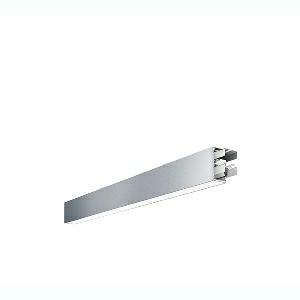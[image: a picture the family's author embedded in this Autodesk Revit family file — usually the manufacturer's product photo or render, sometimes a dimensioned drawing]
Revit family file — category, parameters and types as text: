
# Revit family: dotoo_line_-_dla_1000_840_d_sta_00807949_faaf
name_source: partatom
category: Lighting Fixtures
units: mm (PartAtom-declared; Revit-internal decimal feet)

## family parameters
Cut with Voids When Loaded = No
Host = Face
Light Source = No
Part Type = Normal
Room Calculation Point = No
Round Connector Dimension = Use Diameter
Shared = No

## types (1)
- DOTOO.line - DLA 1000/840/D STA (1 x LED, 1000 lm, 4000K)
    Apparent Load = 10 VA
    Approval mark = CE
    CIE Flux Codes = 67 91 98 100 100
    Color Rendering = 80-89
    Color Temperature = 4000K
    Control Gear = Electronic ballast
    Default Elevation = 1800 mm
    Description = DLA 1000/840/D|Surface-mounted luminaire.|light source: LED|work equipment: Adjustable electronic ballast, digital DALI|connected load: 220-240 V, 50/60 Hz|Power consumption: approx. 9,5 W|luminous flux: 1000 lm|luminous efficacy: 105 lm/W|light distribution: Direct|colour temperature: Cold white, ca. 4000 K|class of protection: I|technology: Continuously dimmable|mains lead: Connector|glare control: Prism aperture|special features: DALI Load 1x, TouchDIM - dimming via standard switch, Through-wired, up to 18 m on one mains connection, Flicker-free, Suitable as emergency lighting, Start luminaire with mains connection, Mechanical and electrical connection of the individual modules without tools|
    Frequency = 50 Hz
    Height = 110 mm
    Lamp = 1 x LED
    Lamp Light Flux = 1000 lm
    Lamp count = 1
    Length = 848 mm
    Luminous efficacy = 105 lm/W
    Manufacturer = Waldmann
    ModVariant = No
    Model = 00807949
    Mounting Place = Ceiling
    Mounting Type = Surface mounted
    Number of Poles = 1
    OnlyDefault = Yes
    Power Factor = 1
    Product Name = DOTOO.line - DLA 1000/840/D STA
    Product group = Ceiling mounted luminaire
    ProductGroupID = 3
    Protection Class = Protection class I
    Protection Degree = IP 40
    RLX_Detail_Level = 1
    RLX_Emergency_Light_Flux = 0 lm
    RLX_Emergency_Type = 0
    RLX_Emergency_Type_DB = No
    RlxData = <blob elided: 18353 chars, md5=97673f3b>
    Socket = socket
    Standby Power = 0 W
    System Light Flux = 1000 lm
    System Power = 10 W
    Type Comments = Product without accessories
    Type Image = 114372000-00807949.jpg
    URL = http://relux.com
    VarID = ---
    Voltage = 230 V
    Voltage Range = 220-240 V
    Weight = 0.00 kg
    Width = 60 mm

## geometry (parser evidence)
native form markers: Blend x4, Sweep x9
no freeform markers — native parametric forms only
